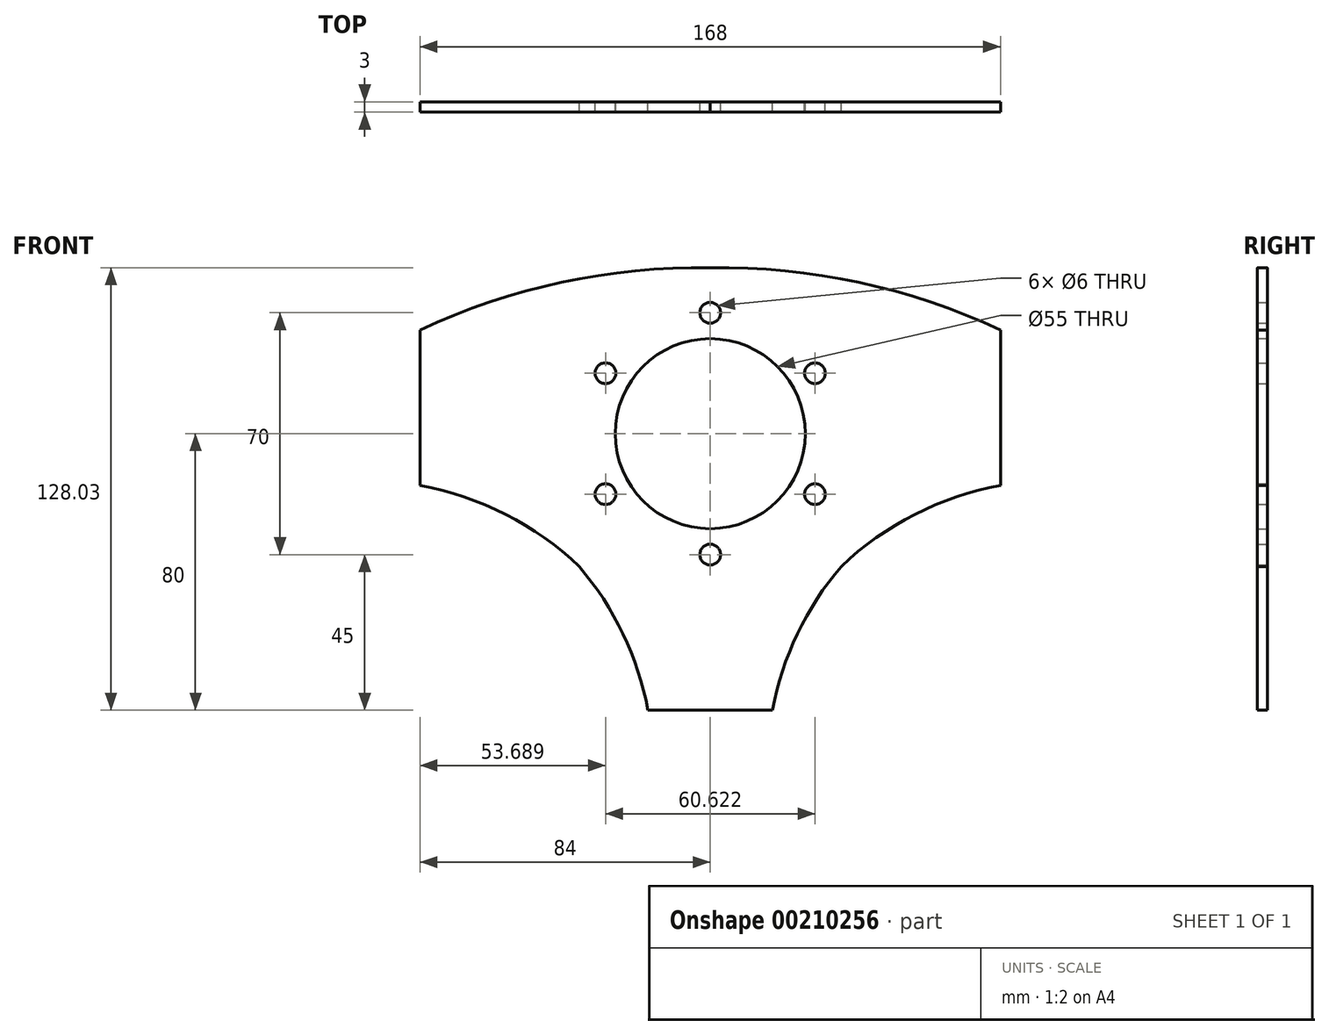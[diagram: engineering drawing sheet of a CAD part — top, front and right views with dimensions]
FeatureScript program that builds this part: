
annotation { "Feature Type Name" : "Feature", "Feature Type Description" : "" }
export const myFeature = defineFeature(function(context is Context, id is Id, definition is map)
    precondition{}
    {
        {
            var Q0;
            Q0=qCreatedBy(makeId("Front.planeOp"),FACE);
            var sketch = newSketch(context, id + "F0", { "sketchPlane" : qUnion([Q0])});
            skCircle(sketch, "E0", {"center": v(0, 0) * mm, "radius": 27.5 * mm});
            skCircle(sketch, "E1", {"center": v(0, 35) * mm, "radius": 3 * mm});
            skCircle(sketch, "E2.1.0", {"center": v(-30.31, 17.5) * mm, "radius": 3 * mm});
            skCircle(sketch, "E2.2.0", {"center": v(-30.31, -17.5) * mm, "radius": 3 * mm});
            skCircle(sketch, "E2.3.0", {"center": v(0, -35) * mm, "radius": 3 * mm});
            skCircle(sketch, "E2.4.0", {"center": v(30.31, -17.5) * mm, "radius": 3 * mm});
            skCircle(sketch, "E2.5.0", {"center": v(30.31, 17.5) * mm, "radius": 3 * mm});
            skLineSegment(sketch, "E3", {"start": v(0, -80) * mm, "end": v(-18, -80) * mm});
            skArc(sketch, "E4", {"start": v(-37.9, -38.47) * mm, "mid": v(-59.22, -23.35) * mm, "end": v(-84, -15) * mm});
            skArc(sketch, "E5", {"start": v(-18, -80) * mm, "mid": v(-25.25, -57.94) * mm, "end": v(-37.9, -38.47) * mm});
            skLineSegment(sketch, "E6", {"start": v(-84, 30) * mm, "end": v(-84, -15) * mm});
            skArc(sketch, "E7", {"start": v(0, 48) * mm, "mid": v(-43.03, 43.8) * mm, "end": v(-84, 30) * mm});
            skArc(sketch, "E8.MirrorCS", {"start": v(0, 48) * mm, "mid": v(43.03, 43.8) * mm, "end": v(84, 30) * mm});
            skLineSegment(sketch, "E9.MirrorCS", {"start": v(84, 30) * mm, "end": v(84, -15) * mm});
            skLineSegment(sketch, "E10.MirrorCS", {"start": v(84, -15) * mm, "end": v(84, -15) * mm});
            skArc(sketch, "E11.MirrorCS", {"start": v(37.9, -38.47) * mm, "mid": v(59.22, -23.35) * mm, "end": v(84, -15) * mm});
            skArc(sketch, "E12.MirrorCS", {"start": v(18, -80) * mm, "mid": v(25.25, -57.94) * mm, "end": v(37.9, -38.47) * mm});
            skLineSegment(sketch, "E13.MirrorCS", {"start": v(0, -80) * mm, "end": v(18, -80) * mm});
            skLineSegment(sketch, "E14", {"start": v(0, 0) * mm, "end": v(37.9, -38.47) * mm});
            skSolve(sketch);
        }
        {
            var Q0;
            Q0=makeQuery(id+"F0.imprint","IMPRINT",FACE,{"disambiguationData":[TD([[makeQuery(id+"F0.imprint","IMPRINT",EDGE,{"derivedFrom":sQuery(id+"F0.wireOp",EDGE,"xvLfkQ3F-fgjy-q9Nn-lcfM-oA4vtxVeLGYN")}),-1.0]])]});
            var Q1;
            {var subQ0=sQuery(id+"F0.wireOp",EDGE,"IXeQJo4f-0NGN-wymH-wL35-tD5XUzaEt9Ii");Q1=makeQuery(id+"F0.imprint","IMPRINT",FACE,{"disambiguationData":[TD([[makeQuery(id+"F0.imprint","IMPRINT",EDGE,{"derivedFrom":subQ0}),-1.0]])]});}
            var Q2;
            Q2=makeQuery(id+"F0.imprint","IMPRINT",FACE,{"disambiguationData":[TD([[makeQuery(id+"F0.imprint","IMPRINT",EDGE,{"derivedFrom":sQuery(id+"F0.wireOp",EDGE,"E0")}),-1.0]])]});
            var Q3;
            {var subQ0=sQuery(id+"F0.wireOp",EDGE,"U97vX6Bn-T6Nm-C19i-UCoZ-bPOguSU8hI4x");Q3=makeQuery(id+"F0.imprint","IMPRINT",FACE,{"disambiguationData":[TD([[makeQuery(id+"F0.imprint","IMPRINT",EDGE,{"derivedFrom":subQ0}),-1.0]])]});}
            var Q4;
            Q4=makeQuery(id+"F0.imprint","IMPRINT",FACE,{"disambiguationData":[TD([[makeQuery(id+"F0.imprint","IMPRINT",EDGE,{"derivedFrom":sQuery(id+"F0.wireOp",EDGE,"iTDH6eJd-3ZuL-mUN2-QFPx-3khqCnK7DwfM")}),-1.0]])]});
            var Q5;
            {var subQ0=sQuery(id+"F0.wireOp",EDGE,"LSPlpz0O-uzcR-zpDg-bx14-Tm5pNzSKurLG");Q5=makeQuery(id+"F0.imprint","IMPRINT",FACE,{"disambiguationData":[TD([[makeQuery(id+"F0.imprint","IMPRINT",EDGE,{"derivedFrom":subQ0}),-1.0]])]});}
            var Q6;
            Q6=makeQuery(id+"F0.imprint","IMPRINT",FACE,{"disambiguationData":[TD([[makeQuery(id+"F0.imprint","IMPRINT",EDGE,{"derivedFrom":sQuery(id+"F0.wireOp",EDGE,"9da5268f-547f-4821-a759-cff2299c6b0c0.MirrorC")}),1.0]])]});
            var Q7;
            Q7=makeQuery(id+"F0.imprint","IMPRINT",FACE,{"disambiguationData":[TD([[makeQuery(id+"F0.imprint","IMPRINT",EDGE,{"derivedFrom":sQuery(id+"F0.wireOp",EDGE,"5ea91802-01c1-4fcd-b629-e54decbf77210.MirrorC")}),1.0]])]});
            extrude(context, id + "F1", {"entities" : qUnion([Q0, Q1, Q2, Q3, Q4, Q5, Q6, Q7]), "depth" : 3 * mm});
        }
    });
